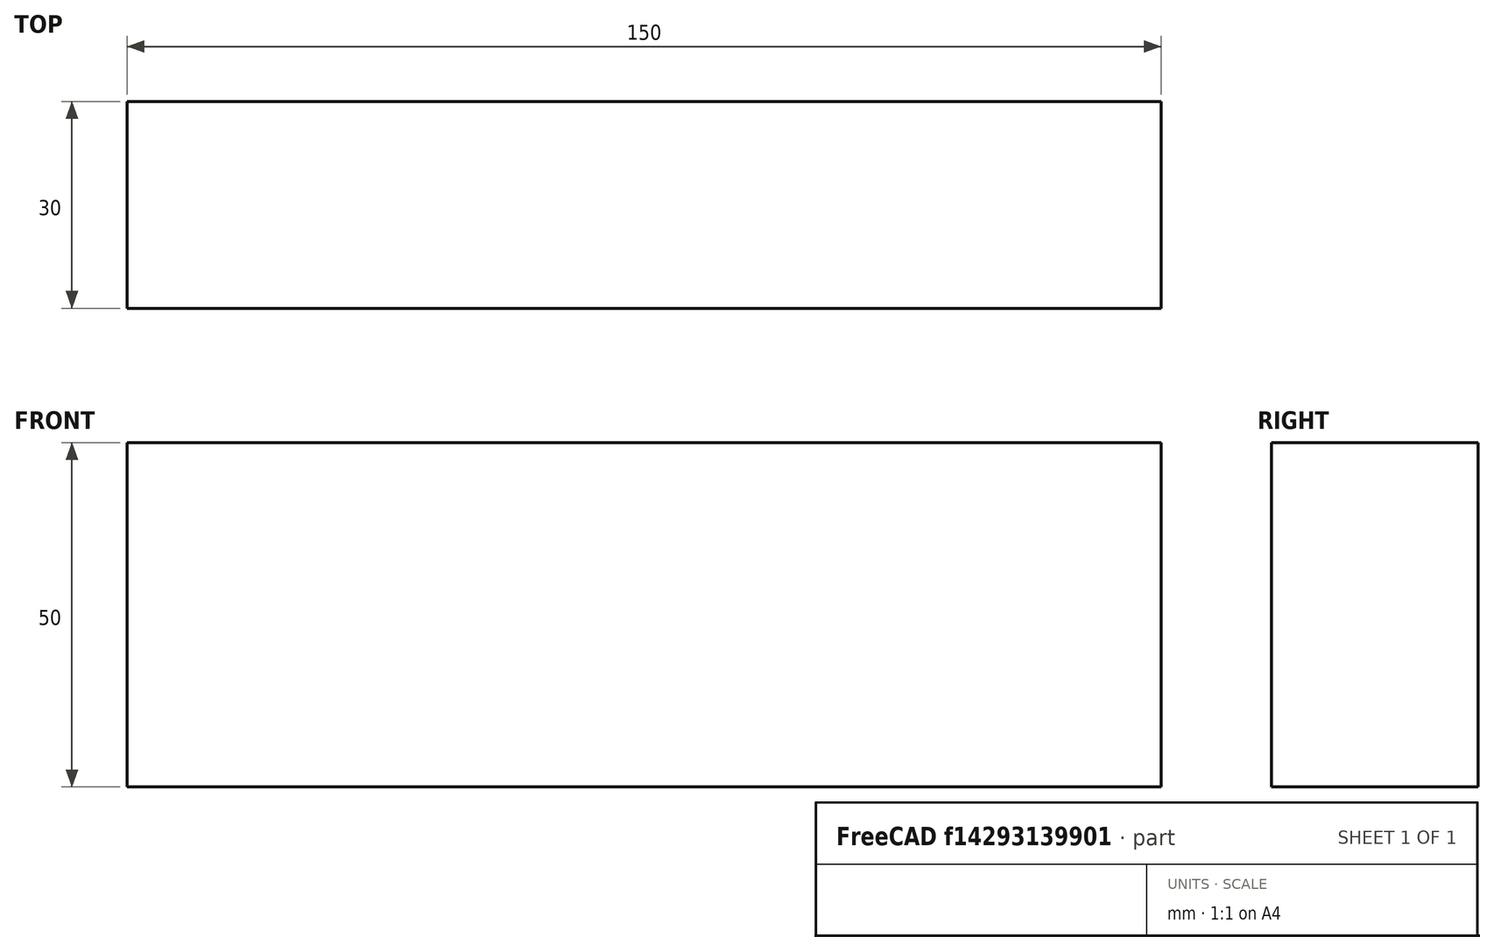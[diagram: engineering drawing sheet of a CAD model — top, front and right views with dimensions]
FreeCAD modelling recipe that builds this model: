
FCSTD DOCUMENT  (FreeCAD 0.15R4671 (Git))
Label: Flat Bar 150x30 EN10058 S235JR
License: All rights reserved
LicenseURL: http://en.wikipedia.org/wiki/All_rights_reserved
objects: Sketcher::SketchObject×1, Part::Extrusion×1
note: 2 computed .brp shape members not serialized (recipe doc carries the construction recipe); baked Part::Feature solids carry a one-line shape summary decoded from their .brp

FEATURE [Sketcher::SketchObject] Sketch
  sketch-geometry (4):
    g0: LineSegment StartX=-75 StartY=-15 StartZ=0 EndX=75 EndY=-15 EndZ=0
    g1: LineSegment StartX=75 StartY=-15 StartZ=0 EndX=75 EndY=15 EndZ=0
    g2: LineSegment StartX=75 StartY=15 StartZ=0 EndX=-75 EndY=15 EndZ=0
    g3: LineSegment StartX=-75 StartY=15 StartZ=0 EndX=-75 EndY=-15 EndZ=0
  constraints (12):
    c: Coincident(g0,g1)
    c: Coincident(g1,g2)
    c: Coincident(g2,g3)
    c: Coincident(g3,g0)
    c: Horizontal(g0)
    c: Horizontal(g2)
    c: Vertical(g1)
    c: Vertical(g3)
    c: Symmetric(g1,g2,g-2)
    c: Symmetric(g0,g1,g-1)
    c: DistanceY(g1) = 30
    c: DistanceX(g0) = 150
FEATURE [Part::Extrusion] Extrude  label="Flat Bar 150x30 EN10058 S235JR"
  Base = -> Sketch
  Dir = (0,0,50)
  Solid = true
